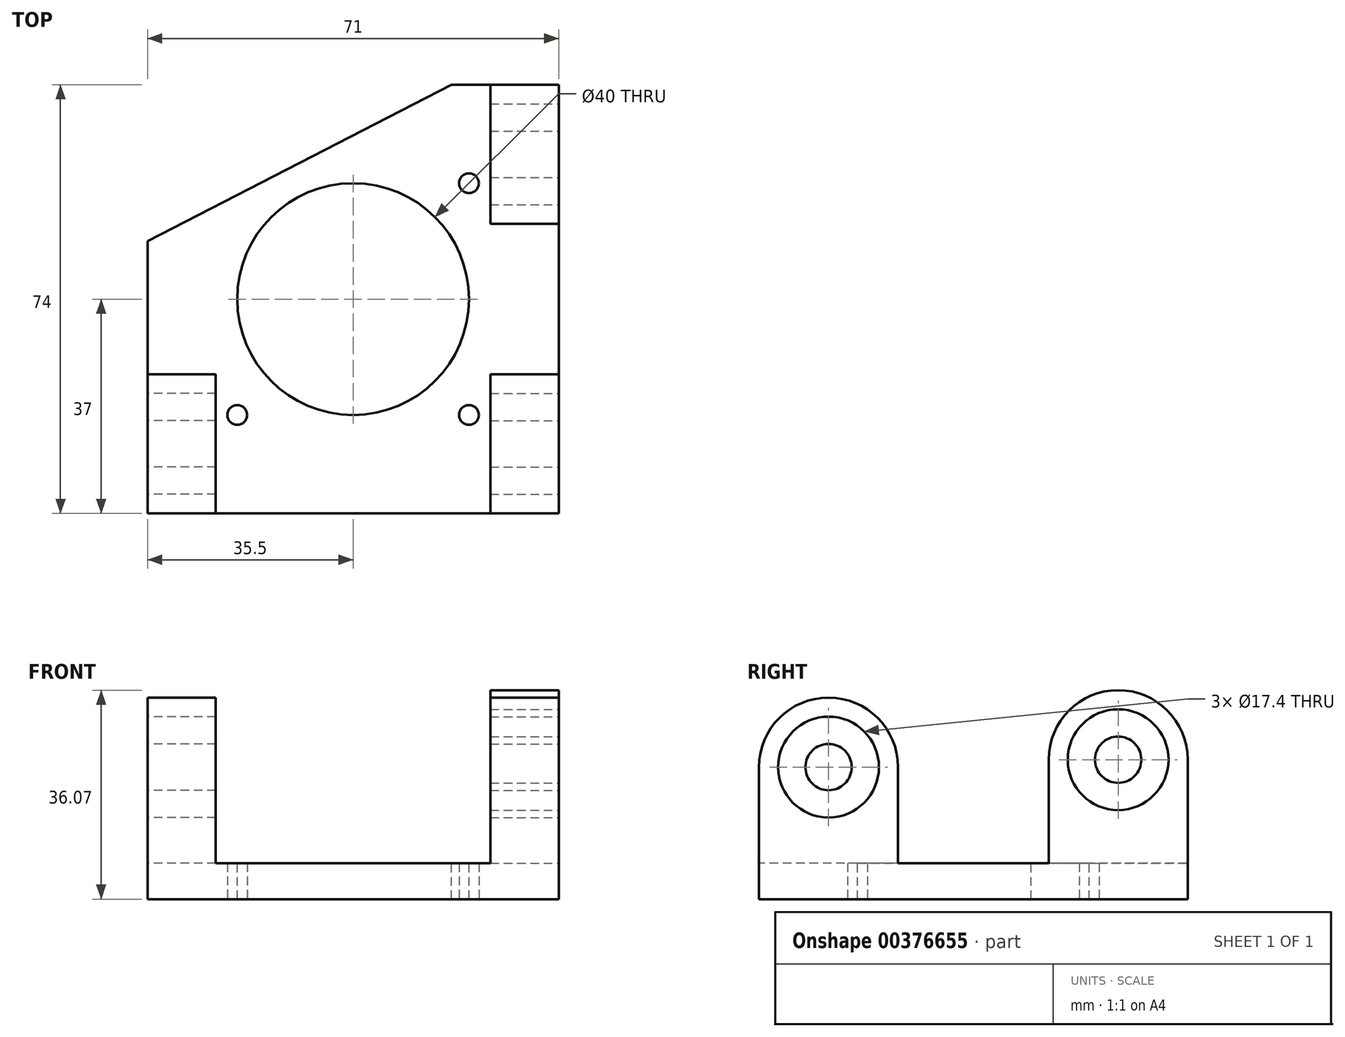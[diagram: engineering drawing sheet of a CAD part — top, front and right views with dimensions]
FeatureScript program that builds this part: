
annotation { "Feature Type Name" : "Feature", "Feature Type Description" : "" }
export const myFeature = defineFeature(function(context is Context, id is Id, definition is map)
    precondition{}
    {
        {
            var Q0;
            Q0=qCreatedBy(makeId("Top.planeOp"),FACE);
            var sketch = newSketch(context, id + "F0", { "sketchPlane" : qUnion([Q0])});
            skLineSegment(sketch, "E0.bottom", {"start": v(17, 37) * mm, "end": v(35.5, 37) * mm});
            skLineSegment(sketch, "E0.top", {"start": v(-35.5, -37) * mm, "end": v(35.5, -37) * mm});
            skLineSegment(sketch, "E0.left", {"start": v(-35.5, 10) * mm, "end": v(-35.5, -37) * mm});
            skLineSegment(sketch, "E0.right", {"start": v(35.5, 37) * mm, "end": v(35.5, -37) * mm});
            skPoint(sketch, "E0.middle", {"position": v(0, 0) * mm});
            skLineSegment(sketch, "E1", {"start": v(-58.98, 25) * mm, "end": v(62.33, 25) * mm, "construction": true});
            skLineSegment(sketch, "E2", {"start": v(-58.98, -25) * mm, "end": v(60.65, -25) * mm, "construction": true});
            skLineSegment(sketch, "E3", {"start": v(46.4, 25) * mm, "end": v(46.4, 0) * mm, "construction": true});
            skLineSegment(sketch, "E4", {"start": v(46.4, -25) * mm, "end": v(46.4, 0) * mm, "construction": true});
            skLineSegment(sketch, "E5", {"start": v(-35.5, 10) * mm, "end": v(17, 37) * mm});
            skCircle(sketch, "E6", {"center": v(0, 0) * mm, "radius": 20 * mm});
            skPoint(sketch, "E7.orphan", {"position": v(-35.5, 37) * mm});
            skSolve(sketch);
        }
        {
            var Q0;
            Q0=makeQuery(id+"F0.imprint","IMPRINT",FACE,{"disambiguationData":[TD([[makeQuery(id+"F0.imprint","IMPRINT",EDGE,{"derivedFrom":sQuery(id+"F0.wireOp",EDGE,"E0.bottom")}),-1.0]])]});
            extrude(context, id + "F1", {"entities" : qUnion([Q0]), "oppositeDirection" : true, "depth" : 6.2 * mm, "offsetDistance" : 25 * mm});
        }
        {
            var Q0;
            Q0=makeQuery(id+"F1.opExtrude","SWEPT_FACE",FACE,{"disambiguationData":[OSD([sQuery(id+"F0.wireOp",EDGE,"E0.right")])]});
            var sketch = newSketch(context, id + "F2", { "sketchPlane" : qUnion([Q0])});
            skCircle(sketch, "E8", {"center": v(-25, 16.6) * mm, "radius": 4 * mm});
            skCircle(sketch, "E9", {"center": v(25, 17.87) * mm, "radius": 4 * mm});
            skCircle(sketch, "E10", {"center": v(-25, 16.6) * mm, "radius": 8.7 * mm});
            skCircle(sketch, "E11", {"center": v(25, 17.87) * mm, "radius": 8.7 * mm});
            skLineSegment(sketch, "E12", {"start": v(-25, 16.6) * mm, "end": v(-25, -14.47) * mm, "construction": true});
            skLineSegment(sketch, "E13", {"start": v(25, 17.87) * mm, "end": v(25, -11.45) * mm, "construction": true});
            skLineSegment(sketch, "E14.top", {"start": v(-37, 0) * mm, "end": v(-13, 0) * mm});
            skLineSegment(sketch, "E14.left", {"start": v(-37, 16.6) * mm, "end": v(-37, 0) * mm});
            skLineSegment(sketch, "E14.right", {"start": v(-13, 16.6) * mm, "end": v(-13, 0) * mm});
            skLineSegment(sketch, "E15.top", {"start": v(13, 0) * mm, "end": v(37, 0) * mm});
            skLineSegment(sketch, "E15.left", {"start": v(13, 17.87) * mm, "end": v(13, 0) * mm});
            skLineSegment(sketch, "E15.right", {"start": v(37, 17.87) * mm, "end": v(37, 0) * mm});
            skArc(sketch, "E16", {"start": v(-13, 16.6) * mm, "mid": v(-25, 28.6) * mm, "end": v(-37, 16.6) * mm});
            skArc(sketch, "E17", {"start": v(37, 17.87) * mm, "mid": v(25, 29.87) * mm, "end": v(13, 17.87) * mm});
            skSolve(sketch);
        }
        {
            var Q0;
            Q0 = qSketchRegion(id + "F2", true);
            extrude(context, id + "F3", {"entities" : qUnion([Q0]), "operationType" : NewBodyOperationType.ADD, "oppositeDirection" : true, "depth" : 11.8 * mm, "offsetDistance" : 25 * mm});
        }
        {
            var Q0;
            Q0=makeQuery(id+"F2.imprint","IMPRINT",FACE,{"disambiguationData":[TD([[makeQuery(id+"F2.imprint","IMPRINT",EDGE,{"derivedFrom":sQuery(id+"F2.wireOp",EDGE,"E8")}),-1.0]])]});
            var Q1;
            Q1=makeQuery(id+"F2.imprint","IMPRINT",FACE,{"disambiguationData":[TD([[makeQuery(id+"F2.imprint","IMPRINT",EDGE,{"derivedFrom":sQuery(id+"F2.wireOp",EDGE,"E9")}),-1.0]])]});
            var Q2;
            Q2=makeQuery(id+"F3.opExtrude","CAP_FACE",FACE,{"disambiguationData":[OSD([sQuery(id+"F2.wireOp",EDGE,"E10"),sQuery(id+"F2.wireOp",EDGE,"E14.top"),sQuery(id+"F2.wireOp",EDGE,"E14.left"),sQuery(id+"F2.wireOp",EDGE,"E14.right"),sQuery(id+"F2.wireOp",EDGE,"E16")])],"isStart":false});
            extrude(context, id + "F4", {"entities" : qUnion([Q0, Q1]), "endBound" : BoundingType.UP_TO_SURFACE, "oppositeDirection" : true, "depth" : 25 * mm, "endBoundEntityFace" : qUnion([Q2]), "offsetDistance" : 25 * mm});
        }
        {
            var Q0;
            Q0=makeQuery(id+"F1.opExtrude","SWEPT_FACE",FACE,{"disambiguationData":[OSD([sQuery(id+"F0.wireOp",EDGE,"E0.left")])]});
            var sketch = newSketch(context, id + "F5", { "sketchPlane" : qUnion([Q0])});
            skLineSegment(sketch, "E18.0.0", {"start": v(13, 16.6) * mm, "end": v(13, 0) * mm});
            skLineSegment(sketch, "E18.0.1", {"start": v(13, 0) * mm, "end": v(37, 0) * mm});
            skLineSegment(sketch, "E18.0.2", {"start": v(37, 0) * mm, "end": v(37, 16.6) * mm});
            skArc(sketch, "E18.0.3", {"start": v(37, 16.6) * mm, "mid": v(25, 28.6) * mm, "end": v(13, 16.6) * mm});
            skCircle(sketch, "E19.0.0", {"center": v(25, 16.6) * mm, "radius": 8.7 * mm});
            skCircle(sketch, "E20.0", {"center": v(25, 16.6) * mm, "radius": 4 * mm});
            skSolve(sketch);
        }
        {
            var Q0;
            Q0=makeQuery(id+"F5.imprint","IMPRINT",FACE,{"disambiguationData":[TD([[makeQuery(id+"F5.imprint","IMPRINT",EDGE,{"derivedFrom":sQuery(id+"F5.wireOp",EDGE,"E18.0.0")}),1.0]])]});
            extrude(context, id + "F6", {"entities" : qUnion([Q0]), "operationType" : NewBodyOperationType.ADD, "oppositeDirection" : true, "depth" : 11.8 * mm, "offsetDistance" : 25 * mm});
        }
        {
            var Q0;
            Q0=makeQuery(id+"F5.imprint","IMPRINT",FACE,{"disambiguationData":[TD([[makeQuery(id+"F5.imprint","IMPRINT",EDGE,{"derivedFrom":sQuery(id+"F5.wireOp",EDGE,"E19.0.0")}),1.0]])]});
            var Q1;
            Q1=makeQuery(id+"F6.opExtrude","CAP_FACE",FACE,{"disambiguationData":[OSD([sQuery(id+"F5.wireOp",EDGE,"E18.0.0"),sQuery(id+"F5.wireOp",EDGE,"E18.0.1"),sQuery(id+"F5.wireOp",EDGE,"E18.0.2"),sQuery(id+"F5.wireOp",EDGE,"E18.0.3"),sQuery(id+"F5.wireOp",EDGE,"E19.0.0")])],"isStart":false});
            extrude(context, id + "F7", {"entities" : qUnion([Q0]), "endBound" : BoundingType.UP_TO_SURFACE, "oppositeDirection" : true, "depth" : 25 * mm, "endBoundEntityFace" : qUnion([Q1]), "offsetDistance" : 25 * mm});
        }
        {
            var Q0;
            Q0=makeQuery(id+"F1.opExtrude","CAP_FACE",FACE,{"disambiguationData":[OSD([sQuery(id+"F0.wireOp",EDGE,"E0.bottom"),sQuery(id+"F0.wireOp",EDGE,"E0.top"),sQuery(id+"F0.wireOp",EDGE,"E0.left"),sQuery(id+"F0.wireOp",EDGE,"E0.right"),sQuery(id+"F0.wireOp",EDGE,"E5"),sQuery(id+"F0.wireOp",EDGE,"E6")])],"isStart":false});
            var sketch = newSketch(context, id + "F8", { "sketchPlane" : qUnion([Q0])});
            skLineSegment(sketch, "E21.bottom", {"start": v(20, -20) * mm, "end": v(-20, -20) * mm});
            skLineSegment(sketch, "E21.top", {"start": v(20, 20) * mm, "end": v(-20, 20) * mm});
            skLineSegment(sketch, "E21.left", {"start": v(20, -20) * mm, "end": v(20, 20) * mm});
            skLineSegment(sketch, "E21.right", {"start": v(-20, -20) * mm, "end": v(-20, 20) * mm});
            skPoint(sketch, "E21.middle", {"position": v(0, 0) * mm});
            skPoint(sketch, "E22", {"position": v(-20, 20) * mm});
            skPoint(sketch, "E23", {"position": v(20, 20) * mm});
            skPoint(sketch, "E24", {"position": v(20, -20) * mm});
            skSolve(sketch);
        }
        {
            var Q0;
            Q0=sQuery(id+"F8.wireOp",VERTEX,"E22");
            var Q1;
            Q1=sQuery(id+"F8.wireOp",VERTEX,"E23");
            var Q2;
            Q2=sQuery(id+"F8.wireOp",VERTEX,"E24");
            var Q3;
            Q3=makeQuery(id+"F1.opExtrude","SWEPT_BODY",BODY,{"disambiguationData":[OSD([sQuery(id+"F0.wireOp",EDGE,"E0.bottom"),sQuery(id+"F0.wireOp",EDGE,"E0.top"),sQuery(id+"F0.wireOp",EDGE,"E0.left"),sQuery(id+"F0.wireOp",EDGE,"E0.right"),sQuery(id+"F0.wireOp",EDGE,"E5"),sQuery(id+"F0.wireOp",EDGE,"E6")])]});
            var Q4;
            Q4=makeQuery(id+"F7.opExtrude","SWEPT_BODY",BODY,{"disambiguationData":[OSD([sQuery(id+"F5.wireOp",EDGE,"E19.0.0"),sQuery(id+"F5.wireOp",EDGE,"E20.0")])]});
            var Q5;
            Q5=makeQuery(id+"F4.opExtrude","SWEPT_BODY",BODY,{"disambiguationData":[OSD([sQuery(id+"F2.wireOp",EDGE,"E8"),sQuery(id+"F2.wireOp",EDGE,"E10")])]});
            var Q6;
            Q6=makeQuery(id+"F4.opExtrude","SWEPT_BODY",BODY,{"disambiguationData":[OSD([sQuery(id+"F2.wireOp",EDGE,"E9"),sQuery(id+"F2.wireOp",EDGE,"E11")])]});
            hole(context, id + "F9", {"style" : HoleStyle.SIMPLE, "endStyle" : HoleEndStyle.THROUGH, "holeDiameter" : 3.42 * mm, "majorDiameter" : 5 * mm, "tappedDepth" : 12 * mm, "tapClearance" : 3, "startFromSketch" : true, "locations" : qUnion([Q0, Q1, Q2]), "scope" : qUnion([Q3, Q4, Q5, Q6])});
        }
    });
